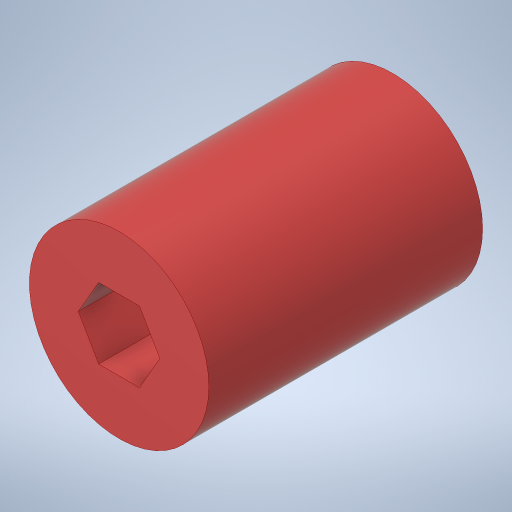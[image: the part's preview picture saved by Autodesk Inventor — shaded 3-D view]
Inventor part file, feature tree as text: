
AUTODESK INVENTOR PART (.ipt)
format: ipt  version: 2023.3 (Build 273359000, 359)  size: 220,160 bytes
history: native  units: in
note: dims shown in document units (in); Inventor stores cm internally (conversion verified against a paired STEP export)
features: extrude x1, sketch x1
ambient origin geometry x8: Origin, YZ Plane, XZ Plane, XY Plane, X Axis, Y Axis, Z Axis, Center Point
bodies: Solid1 (feature_tree)
feature tree (2):
  extrude  "Extrusion1"  Depth=0.5in
  sketch  "Sketch1"  dims[d0=1.27in d1=0.5in d2=1.9375in d3=0.0in]
